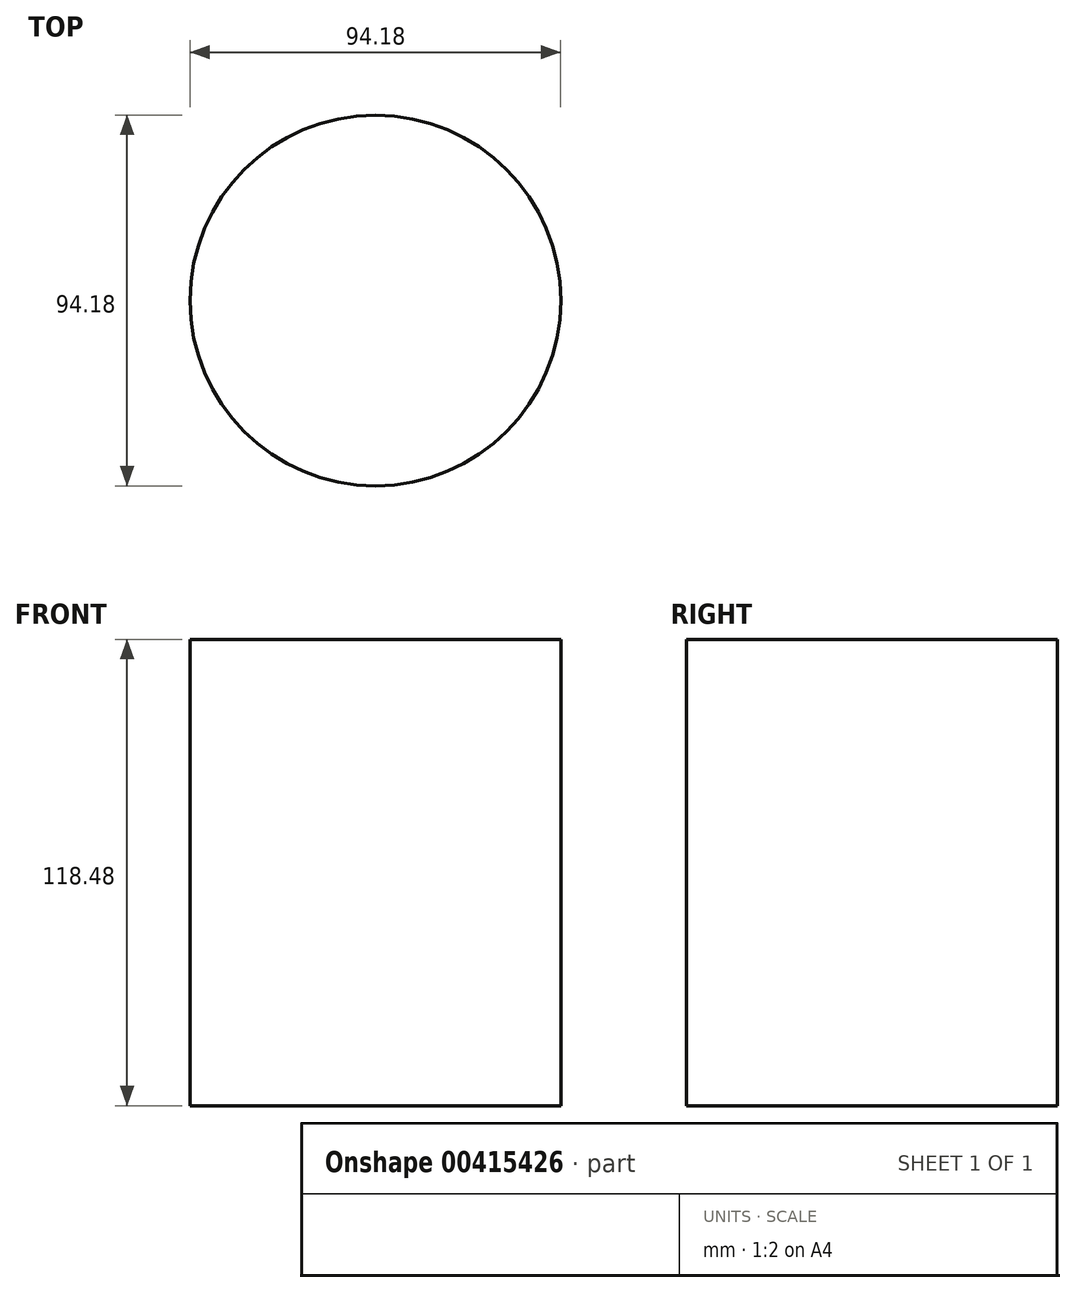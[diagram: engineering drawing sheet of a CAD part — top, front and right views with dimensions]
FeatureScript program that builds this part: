
annotation { "Feature Type Name" : "Feature", "Feature Type Description" : "" }
export const myFeature = defineFeature(function(context is Context, id is Id, definition is map)
    precondition{}
    {
        {
            var Q0;
            Q0=qCreatedBy(makeId("Front.planeOp"),FACE);
            var sketch = newSketch(context, id + "F0", { "sketchPlane" : qUnion([Q0])});
            skLineSegment(sketch, "E0", {"start": v(0, 76.04) * mm, "end": v(0, -76.04) * mm, "construction": true});
            skLineSegment(sketch, "E1", {"start": v(0, -76.04) * mm, "end": v(-47.1, -76.04) * mm});
            skLineSegment(sketch, "E2", {"start": v(-47.1, -76.04) * mm, "end": v(-47.1, 42.44) * mm});
            skLineSegment(sketch, "E3", {"start": v(-47.1, 42.44) * mm, "end": v(0, 42.44) * mm});
            skLineSegment(sketch, "E4", {"start": v(0, 42.44) * mm, "end": v(0, -76.04) * mm});
            skSolve(sketch);
        }
        {
            var Q0;
            Q0=makeQuery(id+"F0.imprint","IMPRINT",FACE,{"disambiguationData":[TD([[makeQuery(id+"F0.imprint","IMPRINT",EDGE,{"derivedFrom":sQuery(id+"F0.wireOp",EDGE,"E1")}),-1.0]])]});
            var Q1;
            Q1=sQuery(id+"F0.wireOp",EDGE,"E0");
            revolve(context, id + "F1", {"entities" : qUnion([Q0]), "axis" : qUnion([Q1]), "revolveType" : RevolveType.FULL});
        }
    });
